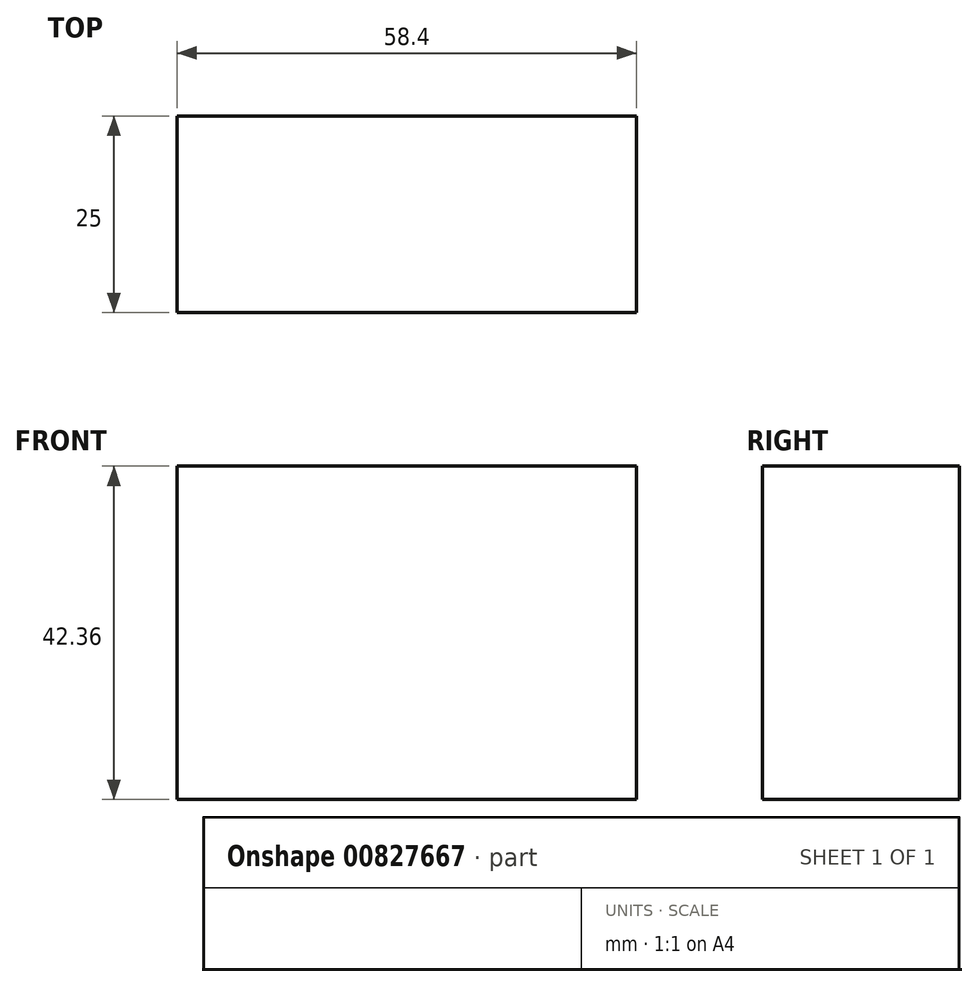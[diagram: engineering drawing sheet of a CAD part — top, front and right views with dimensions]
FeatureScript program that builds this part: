
annotation { "Feature Type Name" : "Feature", "Feature Type Description" : "" }
export const myFeature = defineFeature(function(context is Context, id is Id, definition is map)
    precondition{}
    {
        {
            var Q0;
            Q0=qCreatedBy(makeId("Front.planeOp"),FACE);
            var sketch = newSketch(context, id + "F0", { "sketchPlane" : qUnion([Q0])});
            skLineSegment(sketch, "E0.bottom", {"start": v(29.2, -21.18) * mm, "end": v(-29.2, -21.18) * mm});
            skLineSegment(sketch, "E0.top", {"start": v(29.2, 21.18) * mm, "end": v(-29.2, 21.18) * mm});
            skLineSegment(sketch, "E0.left", {"start": v(29.2, -21.18) * mm, "end": v(29.2, 21.18) * mm});
            skLineSegment(sketch, "E0.right", {"start": v(-29.2, -21.18) * mm, "end": v(-29.2, 21.18) * mm});
            skPoint(sketch, "E0.middle", {"position": v(0, 0) * mm});
            skSolve(sketch);
        }
        {
            var Q0;
            Q0 = qSketchRegion(id + "F0", true);
            extrude(context, id + "F1", {"entities" : qUnion([Q0]), "endBound" : BoundingType.SYMMETRIC, "depth" : 25 * mm, "offsetDistance" : 25 * mm});
        }
    });
